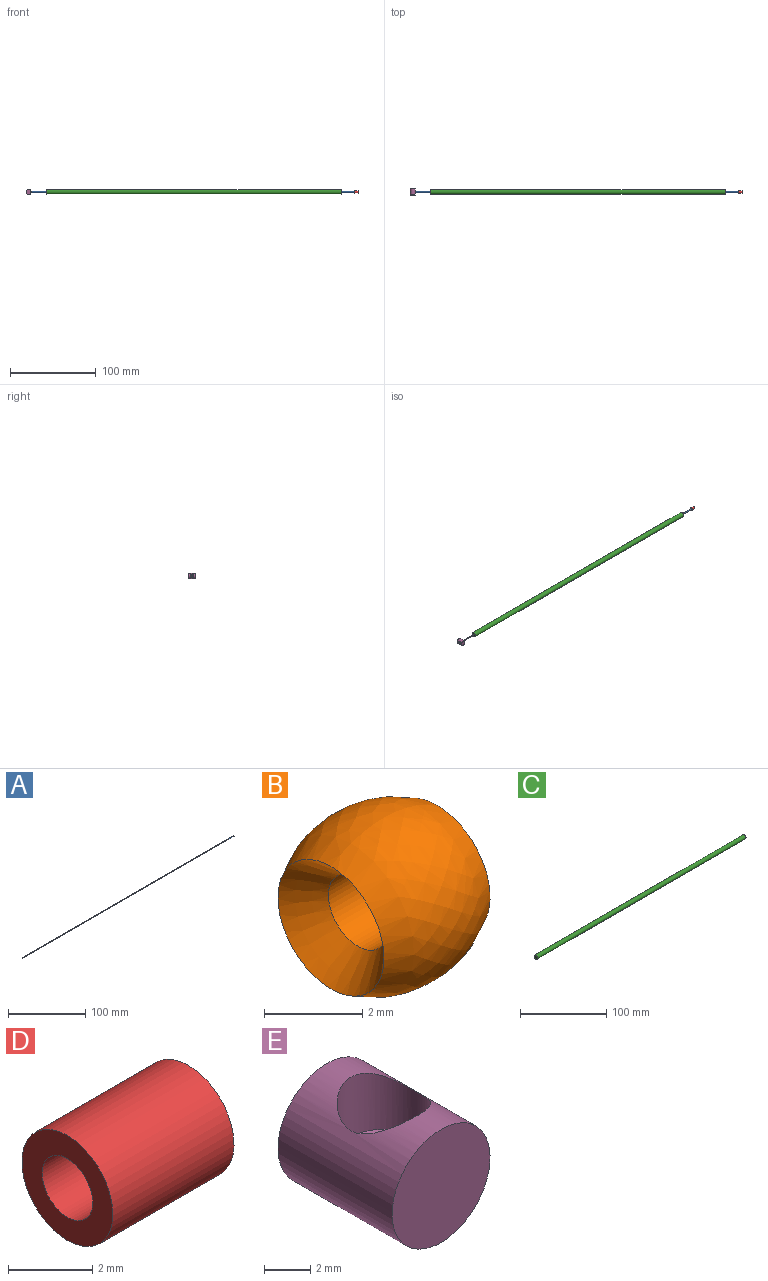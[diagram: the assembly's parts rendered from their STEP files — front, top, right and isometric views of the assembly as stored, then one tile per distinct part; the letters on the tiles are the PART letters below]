
ASSEMBLY  parts=5 mates=5
PART A: 3 faces, bbox 386x1.2x1.2 mm
  f0: plane 1.22x1.22mm, normal (-1,0,0), area 1.2mm2, adj f2
  f1: plane 1.22x1.22mm, normal (1,0,0), area 1.2mm2, adj f2
  f2: cylinder r=0.61mm len=386.03mm, axis (-1,0,0), area 1478.6mm2, adj f0,f1
PART B: 4 faces, bbox 3x4x4 mm
  f0: plane 3.05x3.05mm, normal (1,0,0), area 5mm2, adj f1,f2
  f1: revolved ~3.96x3.96mm, area 37.1mm2, adj f0,f3
  f2: cylinder r=0.85mm len=2.27mm, axis (-1,0,0), area 12.2mm2, adj f0,f3
  f3: cone r=0.85mm half-angle=41deg, axis (-1,0,0), area 7.7mm2, adj f1,f2
PART C: 3 faces, bbox 342.9x5.5x5.5 mm
  f0: plane 5.54x5.54mm, normal (-1,0,0), area 24.1mm2, adj f2
  f1: plane 5.54x5.54mm, normal (1,0,0), area 24.1mm2, adj f2
  f2: cylinder r=2.77mm len=342.9mm, axis (-1,0,0), area 5965mm2, adj f0,f1
PART D: 4 faces, bbox 4.1x3x3 mm
  f0: plane 3.05x3.05mm, normal (-1,0,0), area 5mm2, adj f2,f3
  f1: plane 3.05x3.05mm, normal (1,0,0), area 5mm2, adj f2,f3
  f2: cylinder r=1.52mm len=4.06mm, axis (-1,0,0), area 38.9mm2, adj f0,f1
  f3: cylinder r=0.85mm len=4.06mm, axis (-1,0,0), area 21.7mm2, adj f0,f1
PART E: 6 faces, bbox 6x7x6 mm
  f0: cone r=0mm half-angle=59deg, axis (0,0,1), area 11.8mm2, adj f3,f4
  f1: plane 5.99x5.99mm, normal (0,-1,0), area 28.2mm2, adj f5
  f2: plane 5.99x5.99mm, normal (0,1,0), area 28.2mm2, adj f5
  f3: cylinder r=2.03mm len=4.06mm, axis (0,0,1), area 35.7mm2, adj f0,f5
  f4: cylinder r=0.95mm len=2.17mm, axis (0,0,-1), area 12.5mm2, adj f0,f5
  f5: cylinder r=3mm len=6.99mm, axis (0,-1,0), area 114.8mm2, adj f1,f2,f3,f4
PLACE A t=(-78.7,41.15,-32.16)mm
PLACE B t=(-78.7,41.15,-32.16)mm
PLACE C t=(-55.02,41.15,-32.16)mm
PLACE D t=(303.26,41.15,-32.16)mm
PLACE E rot(axis=(0.71,0,-0.71),180deg) t=(-72.84,37.66,-29.16)mm
MATE cylindrical D.f2 <-> A.f2  axis (1,0,0) through (307.33,41.15,-32.16)mm
MATE cylindrical B.f2 <-> A.f2  axis (-1,0,0) through (-78.7,41.15,-32.16)mm
MATE cylindrical E.f0 <-> B.f2  axis (-1,0,0) through (-75.66,41.15,-32.16)mm
MATE cylindrical A.f2 <-> C.f2  axis (-1,0,0) through (-78.7,41.15,-32.16)mm
MATE cylindrical D.f2 <-> A.f2  axis (1,0,0) through (307.33,41.15,-32.16)mm
